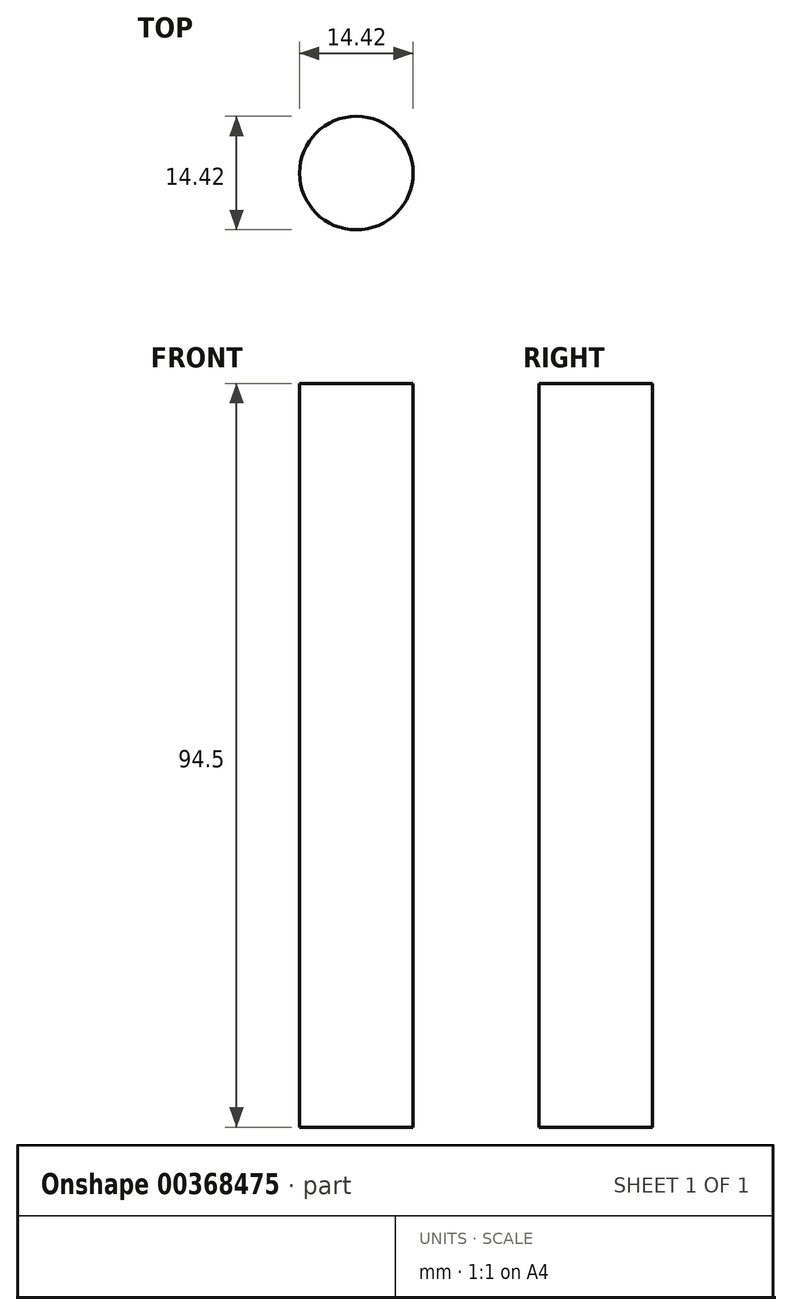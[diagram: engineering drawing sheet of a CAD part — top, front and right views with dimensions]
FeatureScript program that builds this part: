
annotation { "Feature Type Name" : "Feature", "Feature Type Description" : "" }
export const myFeature = defineFeature(function(context is Context, id is Id, definition is map)
    precondition{}
    {
        {
            var Q0;
            Q0=qCreatedBy(makeId("Top.planeOp"),FACE);
            var sketch = newSketch(context, id + "F0", { "sketchPlane" : qUnion([Q0])});
            skCircle(sketch, "E0", {"center": v(0, 0) * mm, "radius": 7.21 * mm});
            skSolve(sketch);
        }
        {
            var Q0;
            Q0 = qSketchRegion(id + "F0", true);
            extrude(context, id + "F1", {"entities" : qUnion([Q0]), "depth" : 94.5 * mm});
        }
    });
